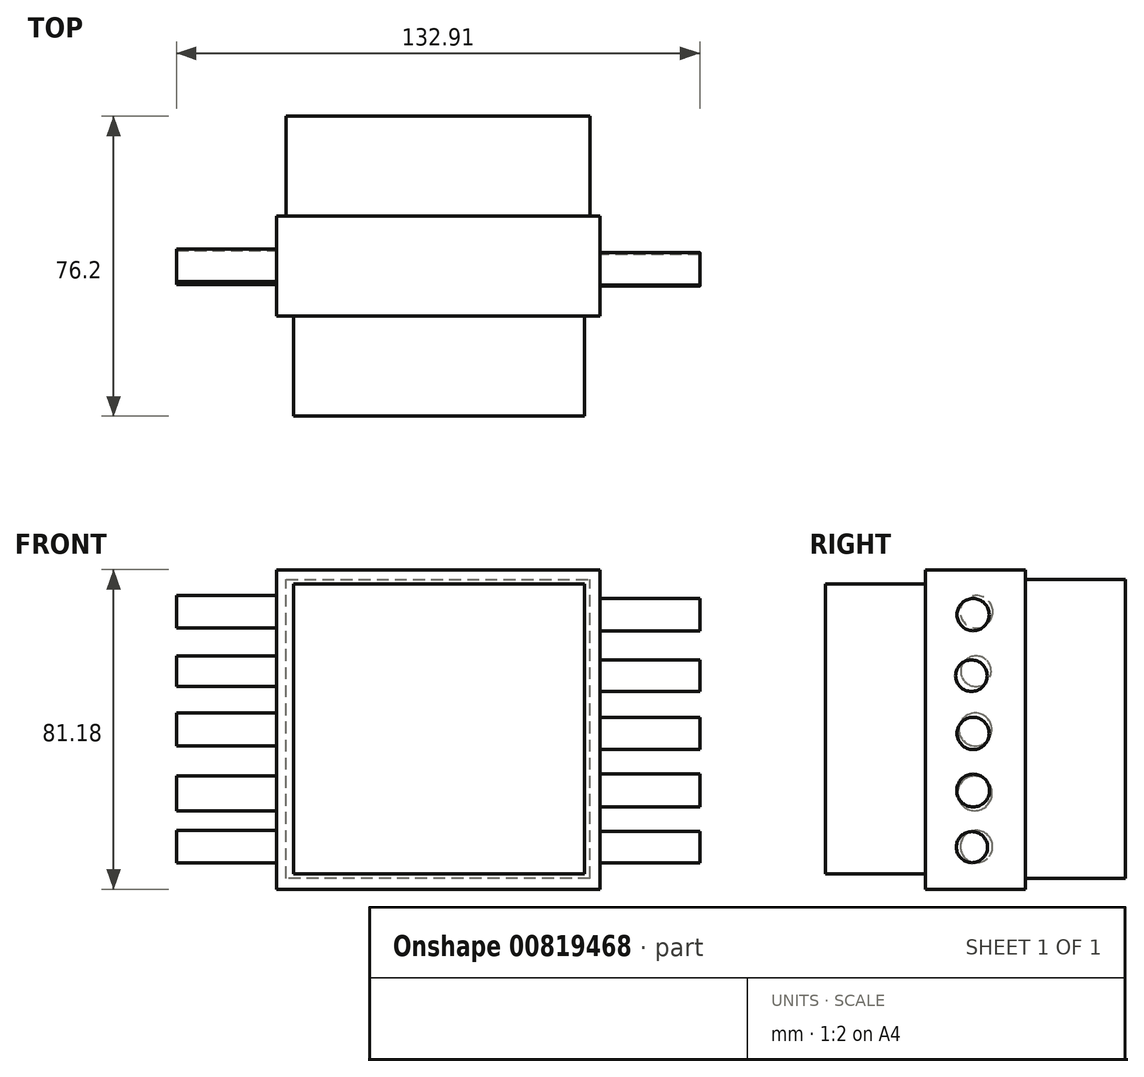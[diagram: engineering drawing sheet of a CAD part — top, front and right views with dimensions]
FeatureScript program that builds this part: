
annotation { "Feature Type Name" : "Feature", "Feature Type Description" : "" }
export const myFeature = defineFeature(function(context is Context, id is Id, definition is map)
    precondition{}
    {
        {
            var Q0;
            Q0=qCreatedBy(makeId("Front.planeOp"),FACE);
            var sketch = newSketch(context, id + "F0", { "sketchPlane" : qUnion([Q0])});
            skLineSegment(sketch, "E0.bottom", {"start": v(0, 0) * mm, "end": v(42.34, 0) * mm});
            skLineSegment(sketch, "E0.top", {"start": v(0, 39.56) * mm, "end": v(42.34, 39.56) * mm});
            skLineSegment(sketch, "E0.left", {"start": v(0, 0) * mm, "end": v(0, 39.56) * mm});
            skLineSegment(sketch, "E0.right", {"start": v(42.34, 0) * mm, "end": v(42.34, 39.56) * mm});
            skLineSegment(sketch, "E1.bottom", {"start": v(0, 0) * mm, "end": v(-39.77, 0) * mm});
            skLineSegment(sketch, "E1.top", {"start": v(0, -41.62) * mm, "end": v(-39.77, -41.62) * mm});
            skLineSegment(sketch, "E1.left", {"start": v(0, 0) * mm, "end": v(0, -41.62) * mm});
            skLineSegment(sketch, "E1.right", {"start": v(-39.77, 0) * mm, "end": v(-39.77, -41.62) * mm});
            skLineSegment(sketch, "E2.top", {"start": v(0, 39.56) * mm, "end": v(-39.77, 39.56) * mm});
            skLineSegment(sketch, "E2.right", {"start": v(-39.77, 0) * mm, "end": v(-39.77, 39.56) * mm});
            skLineSegment(sketch, "E3.top", {"start": v(0, -41.62) * mm, "end": v(42.34, -41.62) * mm});
            skLineSegment(sketch, "E3.right", {"start": v(42.34, 0) * mm, "end": v(42.34, -41.62) * mm});
            skSolve(sketch);
        }
        {
            var Q0;
            Q0=makeQuery(id+"F0.imprint","IMPRINT",FACE,{"disambiguationData":[TD([[makeQuery(id+"F0.imprint","IMPRINT",EDGE,{"derivedFrom":sQuery(id+"F0.wireOp",EDGE,"E0.top")}),-1.0]])]});
            var Q1;
            Q1=makeQuery(id+"F0.imprint","IMPRINT",FACE,{"disambiguationData":[TD([[makeQuery(id+"F0.imprint","IMPRINT",EDGE,{"derivedFrom":sQuery(id+"F0.wireOp",EDGE,"E1.top")}),-1.0]])]});
            var Q2;
            Q2=makeQuery(id+"F0.imprint","IMPRINT",FACE,{"disambiguationData":[TD([[makeQuery(id+"F0.imprint","IMPRINT",EDGE,{"derivedFrom":sQuery(id+"F0.wireOp",EDGE,"E0.bottom")}),-1.0]])]});
            var Q3;
            Q3=makeQuery(id+"F0.imprint","IMPRINT",FACE,{"disambiguationData":[TD([[makeQuery(id+"F0.imprint","IMPRINT",EDGE,{"derivedFrom":sQuery(id+"F0.wireOp",EDGE,"E1.bottom")}),-1.0]])]});
            extrude(context, id + "F1", {"entities" : qUnion([Q0, Q1, Q2, Q3]), "depth" : 25.4 * mm, "offsetDistance" : 25.4 * mm});
        }
        {
            var Q0;
            Q0=makeQuery(id+"F1.opExtrude","CAP_FACE",FACE,{"disambiguationData":[OSD([sQuery(id+"F0.wireOp",EDGE,"E0.top"),sQuery(id+"F0.wireOp",EDGE,"E0.right"),sQuery(id+"F0.wireOp",EDGE,"E1.top"),sQuery(id+"F0.wireOp",EDGE,"E1.right"),sQuery(id+"F0.wireOp",EDGE,"E2.top"),sQuery(id+"F0.wireOp",EDGE,"E2.right"),sQuery(id+"F0.wireOp",EDGE,"E3.top"),sQuery(id+"F0.wireOp",EDGE,"E3.right")])],"isStart":false});
            var sketch = newSketch(context, id + "F2", { "sketchPlane" : qUnion([Q0])});
            skLineSegment(sketch, "E4.bottom", {"start": v(0, 0) * mm, "end": v(38.45, 0) * mm});
            skLineSegment(sketch, "E4.top", {"start": v(0, 35.89) * mm, "end": v(38.45, 35.89) * mm});
            skLineSegment(sketch, "E4.left", {"start": v(0, 0) * mm, "end": v(0, 35.89) * mm});
            skLineSegment(sketch, "E4.right", {"start": v(38.45, 0) * mm, "end": v(38.45, 35.89) * mm});
            skLineSegment(sketch, "E5.bottom", {"start": v(0, 0) * mm, "end": v(-35.49, 0) * mm});
            skLineSegment(sketch, "E5.top", {"start": v(0, -37.78) * mm, "end": v(-35.49, -37.78) * mm});
            skLineSegment(sketch, "E5.left", {"start": v(0, 0) * mm, "end": v(0, -37.78) * mm});
            skLineSegment(sketch, "E5.right", {"start": v(-35.49, 0) * mm, "end": v(-35.49, -37.78) * mm});
            skLineSegment(sketch, "E6.top", {"start": v(0, 35.89) * mm, "end": v(-35.49, 35.89) * mm});
            skLineSegment(sketch, "E6.right", {"start": v(-35.49, 0) * mm, "end": v(-35.49, 35.89) * mm});
            skLineSegment(sketch, "E7.top", {"start": v(0, -37.78) * mm, "end": v(38.45, -37.78) * mm});
            skLineSegment(sketch, "E7.right", {"start": v(38.45, 0) * mm, "end": v(38.45, -37.78) * mm});
            skSolve(sketch);
        }
        {
            var Q0;
            Q0=makeQuery(id+"F2.imprint","IMPRINT",FACE,{"disambiguationData":[TD([[makeQuery(id+"F2.imprint","IMPRINT",EDGE,{"derivedFrom":sQuery(id+"F2.wireOp",EDGE,"E5.bottom")}),-1.0]])]});
            var Q1;
            Q1=makeQuery(id+"F2.imprint","IMPRINT",FACE,{"disambiguationData":[TD([[makeQuery(id+"F2.imprint","IMPRINT",EDGE,{"derivedFrom":sQuery(id+"F2.wireOp",EDGE,"E4.top")}),-1.0]])]});
            var Q2;
            Q2=makeQuery(id+"F2.imprint","IMPRINT",FACE,{"disambiguationData":[TD([[makeQuery(id+"F2.imprint","IMPRINT",EDGE,{"derivedFrom":sQuery(id+"F2.wireOp",EDGE,"E5.top")}),-1.0]])]});
            var Q3;
            Q3=makeQuery(id+"F2.imprint","IMPRINT",FACE,{"disambiguationData":[TD([[makeQuery(id+"F2.imprint","IMPRINT",EDGE,{"derivedFrom":sQuery(id+"F2.wireOp",EDGE,"E4.bottom")}),-1.0]])]});
            extrude(context, id + "F3", {"entities" : qUnion([Q0, Q1, Q2, Q3]), "operationType" : NewBodyOperationType.ADD, "depth" : 25.4 * mm, "offsetDistance" : 25.4 * mm});
        }
        {
            var Q0;
            Q0=makeQuery(id+"F1.opExtrude","CAP_FACE",FACE,{"disambiguationData":[OSD([sQuery(id+"F0.wireOp",EDGE,"E0.top"),sQuery(id+"F0.wireOp",EDGE,"E0.right"),sQuery(id+"F0.wireOp",EDGE,"E1.top"),sQuery(id+"F0.wireOp",EDGE,"E1.right"),sQuery(id+"F0.wireOp",EDGE,"E2.top"),sQuery(id+"F0.wireOp",EDGE,"E2.right"),sQuery(id+"F0.wireOp",EDGE,"E3.top"),sQuery(id+"F0.wireOp",EDGE,"E3.right")])],"isStart":true});
            var sketch = newSketch(context, id + "F4", { "sketchPlane" : qUnion([Q0])});
            skLineSegment(sketch, "E8.bottom", {"start": v(0, 0) * mm, "end": v(37.3, 0) * mm});
            skLineSegment(sketch, "E8.top", {"start": v(0, 37.06) * mm, "end": v(37.3, 37.06) * mm});
            skLineSegment(sketch, "E8.left", {"start": v(0, 0) * mm, "end": v(0, 37.06) * mm});
            skLineSegment(sketch, "E8.right", {"start": v(37.3, 0) * mm, "end": v(37.3, 37.06) * mm});
            skLineSegment(sketch, "E9.bottom", {"start": v(0, 0) * mm, "end": v(-39.88, 0) * mm});
            skLineSegment(sketch, "E9.top", {"start": v(0, -38.83) * mm, "end": v(-39.88, -38.83) * mm});
            skLineSegment(sketch, "E9.left", {"start": v(0, 0) * mm, "end": v(0, -38.83) * mm});
            skLineSegment(sketch, "E9.right", {"start": v(-39.88, 0) * mm, "end": v(-39.88, -38.83) * mm});
            skLineSegment(sketch, "E10.top", {"start": v(0, 37.06) * mm, "end": v(-39.88, 37.06) * mm});
            skLineSegment(sketch, "E10.right", {"start": v(-39.88, 0) * mm, "end": v(-39.88, 37.06) * mm});
            skLineSegment(sketch, "E11.top", {"start": v(0, -38.83) * mm, "end": v(37.3, -38.83) * mm});
            skLineSegment(sketch, "E11.right", {"start": v(37.3, 0) * mm, "end": v(37.3, -38.83) * mm});
            skSolve(sketch);
        }
        {
            var Q0;
            Q0=makeQuery(id+"F4.imprint","IMPRINT",FACE,{"disambiguationData":[TD([[makeQuery(id+"F4.imprint","IMPRINT",EDGE,{"derivedFrom":sQuery(id+"F4.wireOp",EDGE,"E9.bottom")}),-1.0]])]});
            var Q1;
            Q1=makeQuery(id+"F4.imprint","IMPRINT",FACE,{"disambiguationData":[TD([[makeQuery(id+"F4.imprint","IMPRINT",EDGE,{"derivedFrom":sQuery(id+"F4.wireOp",EDGE,"E8.top")}),-1.0]])]});
            var Q2;
            Q2=makeQuery(id+"F4.imprint","IMPRINT",FACE,{"disambiguationData":[TD([[makeQuery(id+"F4.imprint","IMPRINT",EDGE,{"derivedFrom":sQuery(id+"F4.wireOp",EDGE,"E8.bottom")}),-1.0]])]});
            var Q3;
            Q3=makeQuery(id+"F4.imprint","IMPRINT",FACE,{"disambiguationData":[TD([[makeQuery(id+"F4.imprint","IMPRINT",EDGE,{"derivedFrom":sQuery(id+"F4.wireOp",EDGE,"E9.top")}),-1.0]])]});
            extrude(context, id + "F5", {"entities" : qUnion([Q0, Q1, Q2, Q3]), "operationType" : NewBodyOperationType.ADD, "depth" : 25.4 * mm, "offsetDistance" : 25.4 * mm});
        }
        {
            var Q0;
            Q0=makeQuery(id+"F1.opExtrude","SWEPT_FACE",FACE,{"disambiguationData":[OSD([sQuery(id+"F0.wireOp",EDGE,"E0.right"),sQuery(id+"F0.wireOp",EDGE,"E3.right")])]});
            var sketch = newSketch(context, id + "F6", { "sketchPlane" : qUnion([Q0])});
            skCircle(sketch, "E12", {"center": v(-13.35, 28.15) * mm, "radius": 4.09 * mm});
            skCircle(sketch, "E13", {"center": v(-13.78, 12.62) * mm, "radius": 4 * mm});
            skCircle(sketch, "E14", {"center": v(-13.35, -2.04) * mm, "radius": 4.09 * mm});
            skCircle(sketch, "E15", {"center": v(-13.35, -16.55) * mm, "radius": 4.17 * mm});
            skCircle(sketch, "E16", {"center": v(-13.63, -30.93) * mm, "radius": 3.95 * mm});
            skSolve(sketch);
        }
        {
            var Q0;
            Q0=makeQuery(id+"F6.imprint","IMPRINT",FACE,{"disambiguationData":[TD([[makeQuery(id+"F6.imprint","IMPRINT",EDGE,{"derivedFrom":sQuery(id+"F6.wireOp",EDGE,"E12")}),1.0]])]});
            var Q1;
            Q1=makeQuery(id+"F6.imprint","IMPRINT",FACE,{"disambiguationData":[TD([[makeQuery(id+"F6.imprint","IMPRINT",EDGE,{"derivedFrom":sQuery(id+"F6.wireOp",EDGE,"E13")}),1.0]])]});
            var Q2;
            Q2=makeQuery(id+"F6.imprint","IMPRINT",FACE,{"disambiguationData":[TD([[makeQuery(id+"F6.imprint","IMPRINT",EDGE,{"derivedFrom":sQuery(id+"F6.wireOp",EDGE,"E14")}),1.0]])]});
            var Q3;
            Q3=makeQuery(id+"F6.imprint","IMPRINT",FACE,{"disambiguationData":[TD([[makeQuery(id+"F6.imprint","IMPRINT",EDGE,{"derivedFrom":sQuery(id+"F6.wireOp",EDGE,"E15")}),1.0]])]});
            var Q4;
            Q4=makeQuery(id+"F6.imprint","IMPRINT",FACE,{"disambiguationData":[TD([[makeQuery(id+"F6.imprint","IMPRINT",EDGE,{"derivedFrom":sQuery(id+"F6.wireOp",EDGE,"E16")}),1.0]])]});
            extrude(context, id + "F7", {"entities" : qUnion([Q0, Q1, Q2, Q3, Q4]), "operationType" : NewBodyOperationType.ADD, "depth" : 25.4 * mm, "offsetDistance" : 25.4 * mm});
        }
        {
            var Q0;
            Q0=makeQuery(id+"F1.opExtrude","SWEPT_FACE",FACE,{"disambiguationData":[OSD([sQuery(id+"F0.wireOp",EDGE,"E1.right"),sQuery(id+"F0.wireOp",EDGE,"E2.right")])]});
            var sketch = newSketch(context, id + "F8", { "sketchPlane" : qUnion([Q0])});
            skCircle(sketch, "E17", {"center": v(12.48, 28.86) * mm, "radius": 4.14 * mm});
            skCircle(sketch, "E18", {"center": v(12.63, 13.77) * mm, "radius": 3.87 * mm});
            skCircle(sketch, "E19", {"center": v(12.77, -1.03) * mm, "radius": 4.2 * mm});
            skCircle(sketch, "E20", {"center": v(12.92, -17.27) * mm, "radius": 4.4 * mm});
            skCircle(sketch, "E21", {"center": v(12.48, -30.78) * mm, "radius": 4.09 * mm});
            skSolve(sketch);
        }
        {
            var Q0;
            Q0=makeQuery(id+"F8.imprint","IMPRINT",FACE,{"disambiguationData":[TD([[makeQuery(id+"F8.imprint","IMPRINT",EDGE,{"derivedFrom":sQuery(id+"F8.wireOp",EDGE,"E17")}),1.0]])]});
            var Q1;
            Q1=makeQuery(id+"F8.imprint","IMPRINT",FACE,{"disambiguationData":[TD([[makeQuery(id+"F8.imprint","IMPRINT",EDGE,{"derivedFrom":sQuery(id+"F8.wireOp",EDGE,"E18")}),1.0]])]});
            var Q2;
            Q2=makeQuery(id+"F8.imprint","IMPRINT",FACE,{"disambiguationData":[TD([[makeQuery(id+"F8.imprint","IMPRINT",EDGE,{"derivedFrom":sQuery(id+"F8.wireOp",EDGE,"E19")}),1.0]])]});
            var Q3;
            Q3=makeQuery(id+"F8.imprint","IMPRINT",FACE,{"disambiguationData":[TD([[makeQuery(id+"F8.imprint","IMPRINT",EDGE,{"derivedFrom":sQuery(id+"F8.wireOp",EDGE,"E20")}),1.0]])]});
            var Q4;
            Q4=makeQuery(id+"F8.imprint","IMPRINT",FACE,{"disambiguationData":[TD([[makeQuery(id+"F8.imprint","IMPRINT",EDGE,{"derivedFrom":sQuery(id+"F8.wireOp",EDGE,"E21")}),1.0]])]});
            extrude(context, id + "F9", {"entities" : qUnion([Q0, Q1, Q2, Q3, Q4]), "operationType" : NewBodyOperationType.ADD, "depth" : 25.4 * mm, "offsetDistance" : 25.4 * mm});
        }
    });
